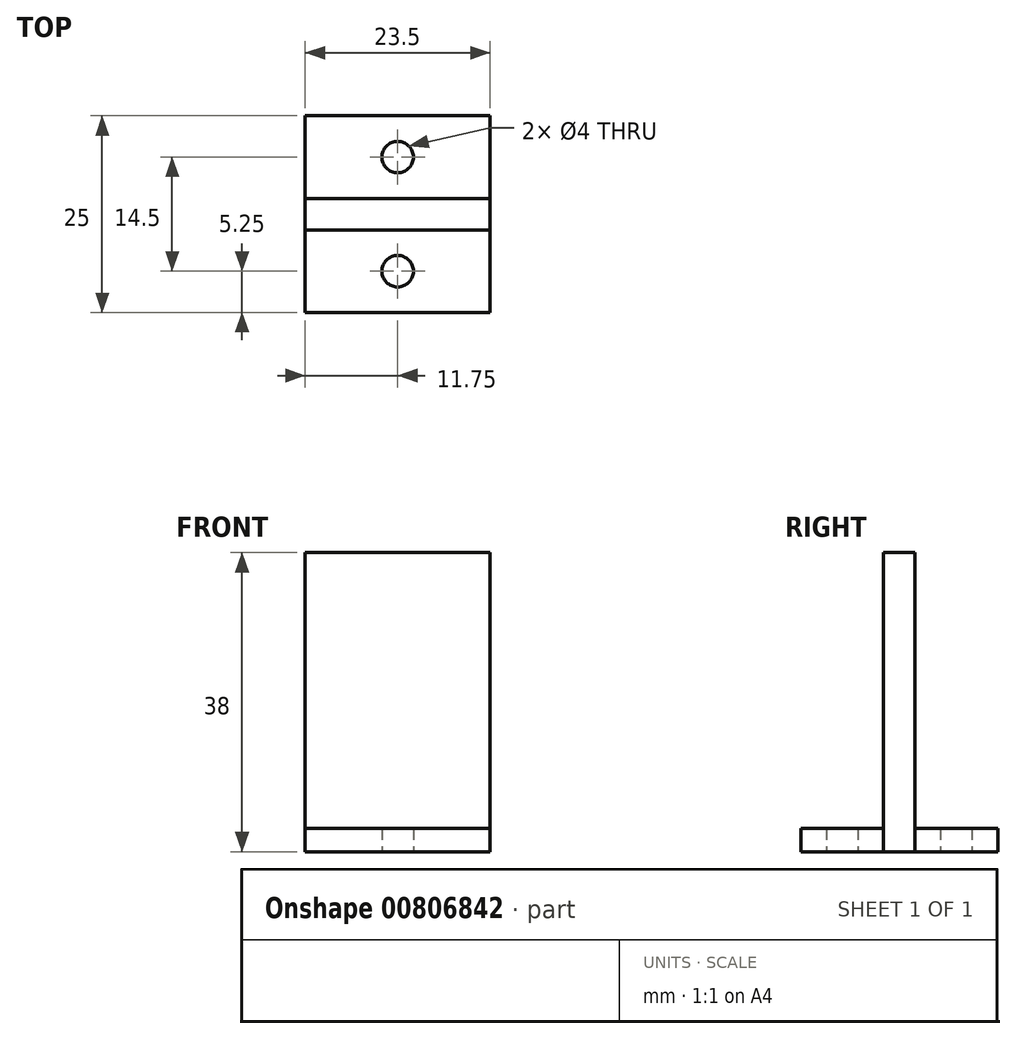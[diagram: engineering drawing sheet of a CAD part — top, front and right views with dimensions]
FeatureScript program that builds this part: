
annotation { "Feature Type Name" : "Feature", "Feature Type Description" : "" }
export const myFeature = defineFeature(function(context is Context, id is Id, definition is map)
    precondition{}
    {
        {
            var Q0;
            Q0=qCreatedBy(makeId("Top.planeOp"),FACE);
            var sketch = newSketch(context, id + "F0", { "sketchPlane" : qUnion([Q0])});
            skLineSegment(sketch, "E0.bottom", {"start": v(11.75, 12.5) * mm, "end": v(-11.75, 12.5) * mm});
            skLineSegment(sketch, "E0.top", {"start": v(11.75, -12.5) * mm, "end": v(-11.75, -12.5) * mm});
            skLineSegment(sketch, "E0.left", {"start": v(11.75, 12.5) * mm, "end": v(11.75, -12.5) * mm});
            skLineSegment(sketch, "E0.right", {"start": v(-11.75, 12.5) * mm, "end": v(-11.75, -12.5) * mm});
            skPoint(sketch, "E0.middle", {"position": v(0, 0) * mm});
            skLineSegment(sketch, "E1.bottom", {"start": v(11.75, 2) * mm, "end": v(-11.75, 2) * mm});
            skLineSegment(sketch, "E1.top", {"start": v(11.75, -2) * mm, "end": v(-11.75, -2) * mm});
            skLineSegment(sketch, "E1.left", {"start": v(11.75, 2) * mm, "end": v(11.75, -2) * mm});
            skLineSegment(sketch, "E1.right", {"start": v(-11.75, 2) * mm, "end": v(-11.75, -2) * mm});
            skLineSegment(sketch, "E2", {"start": v(-11.75, 2) * mm, "end": v(11.75, 12.5) * mm});
            skLineSegment(sketch, "E3", {"start": v(-11.75, -2) * mm, "end": v(11.75, -12.5) * mm});
            skCircle(sketch, "E4", {"center": v(0, -7.25) * mm, "radius": 2 * mm});
            skCircle(sketch, "E5", {"center": v(0, 7.25) * mm, "radius": 2 * mm});
            skSolve(sketch);
        }
        {
            var Q0;
            {var subQ1=sQuery(id+"F0.wireOp",EDGE,"E0.bottom");Q0=makeQuery(id+"F0.imprint","IMPRINT",FACE,{"disambiguationData":[TD([[makeQuery(id+"F0.imprint","IMPRINT",EDGE,{"derivedFrom":subQ1}),1.0]])]});}
            var Q1;
            {var subQ1=sQuery(id+"F0.wireOp",EDGE,"E1.bottom");Q1=makeQuery(id+"F0.imprint","IMPRINT",FACE,{"disambiguationData":[TD([[makeQuery(id+"F0.imprint","IMPRINT",EDGE,{"derivedFrom":subQ1}),-1.0]])]});}
            var Q2;
            {var subQ5=sQuery(id+"F0.wireOp",EDGE,"E0.top");Q2=makeQuery(id+"F0.imprint","IMPRINT",FACE,{"disambiguationData":[TD([[makeQuery(id+"F0.imprint","IMPRINT",EDGE,{"derivedFrom":subQ5}),-1.0]])]});}
            var Q3;
            {var subQ5=sQuery(id+"F0.wireOp",EDGE,"E1.top");Q3=makeQuery(id+"F0.imprint","IMPRINT",FACE,{"disambiguationData":[TD([[makeQuery(id+"F0.imprint","IMPRINT",EDGE,{"derivedFrom":subQ5}),1.0]])]});}
            extrude(context, id + "F1", {"entities" : qUnion([Q0, Q1, Q2, Q3]), "depth" : 3 * mm, "offsetDistance" : 25 * mm});
        }
        {
            var Q0;
            Q0=makeQuery(id+"F0.imprint","IMPRINT",FACE,{"disambiguationData":[TD([[makeQuery(id+"F0.imprint","IMPRINT",EDGE,{"derivedFrom":sQuery(id+"F0.wireOp",EDGE,"E1.bottom")}),1.0]])]});
            extrude(context, id + "F2", {"entities" : qUnion([Q0]), "depth" : 38 * mm, "offsetDistance" : 25 * mm});
        }
    });
